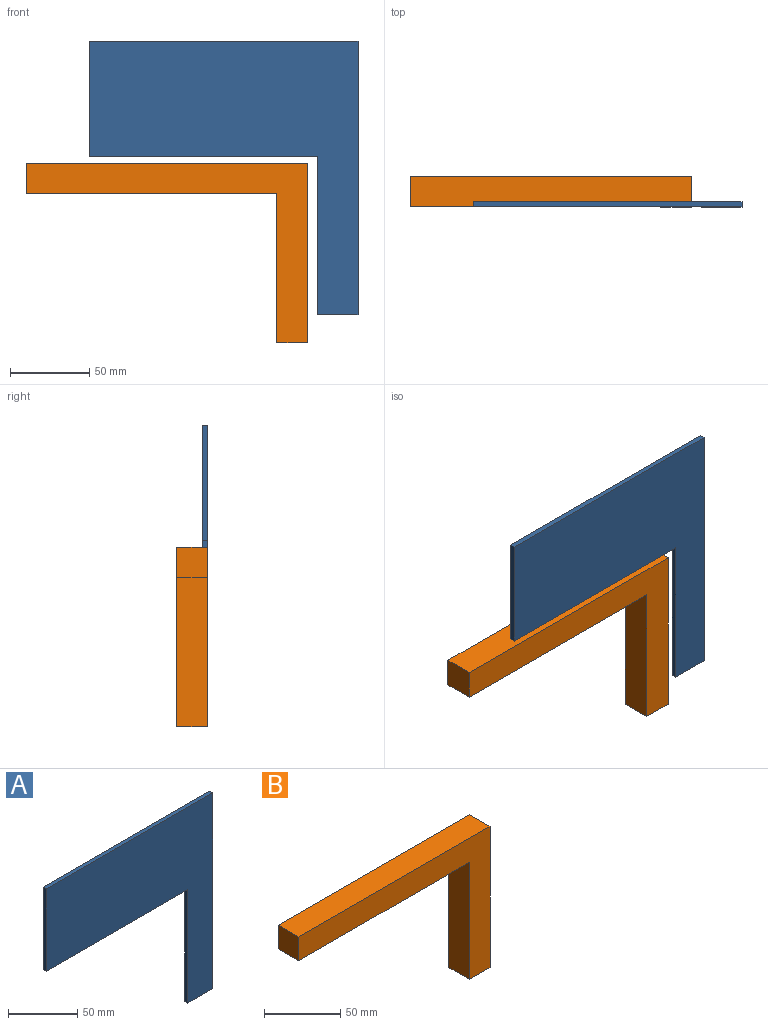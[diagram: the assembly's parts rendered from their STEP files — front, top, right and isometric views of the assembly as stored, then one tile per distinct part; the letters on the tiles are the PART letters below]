
ASSEMBLY  parts=2 mates=1
PART A: 8 faces, bbox 169.4x3.2x172.6 mm
  f0: plane 169.44x3.2mm, normal (0,0,1), area 542.2mm2, adj f1,f5,f6,f7
  f1: plane 72.59x3.2mm, normal (-1,0,0), area 232.3mm2, adj f0,f2,f6,f7
  f2: plane 144.04x3.2mm, normal (0,0,-1), area 460.9mm2, adj f1,f3,f6,f7
  f3: plane 100x3.2mm, normal (-1,0,0), area 320mm2, adj f2,f4,f6,f7
  f4: plane 25.4x3.2mm, normal (0,0,-1), area 81.3mm2, adj f3,f5,f6,f7
  f5: plane 172.59x3.2mm, normal (1,0,0), area 552.3mm2, adj f0,f4,f6,f7
  f6: plane 172.59x169.44mm, normal (0,-1,0), area 14840.3mm2, adj f0,f1,f2,f3,f4,f5
  f7: plane 172.59x169.44mm, normal (0,1,0), area 14840.3mm2, adj f0,f1,f2,f3,f4,f5
PART B: 8 faces, bbox 177.4x19.1x113.2 mm
  f0: plane 113.15x19.05mm, normal (1,0,0), area 2155.6mm2, adj f1,f5,f6,f7
  f1: plane 177.44x19.05mm, normal (0,0,1), area 3380.3mm2, adj f0,f2,f6,f7
  f2: plane 19.05x19.05mm, normal (-1,0,0), area 362.9mm2, adj f1,f3,f6,f7
  f3: plane 158.39x19.05mm, normal (0,0,-1), area 3017.4mm2, adj f2,f4,f6,f7
  f4: plane 94.1x19.05mm, normal (-1,0,0), area 1792.7mm2, adj f3,f5,f6,f7
  f5: plane 19.05x19.05mm, normal (0,0,-1), area 362.9mm2, adj f0,f4,f6,f7
  f6: plane 177.44x113.15mm, normal (0,1,0), area 5173mm2, adj f0,f1,f2,f3,f4,f5
  f7: plane 177.44x113.15mm, normal (0,-1,0), area 5173mm2, adj f0,f1,f2,f3,f4,f5
PLACE A t=(6.72,3.2,-95.66)mm
PLACE B at identity
MATE planar A.f6 <-> B.f7  axis (0,-1,0) through (-40.28,0,25.87)mm
